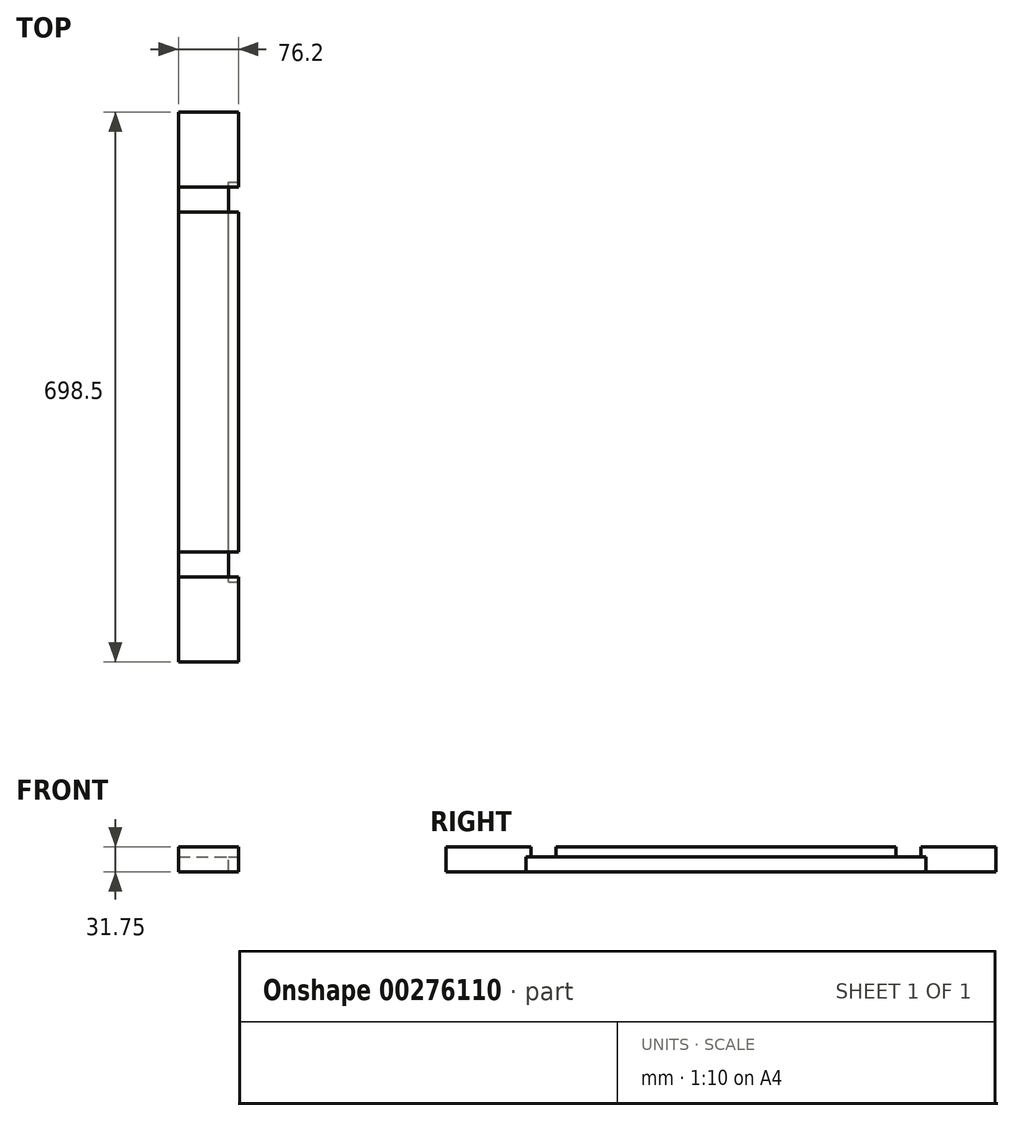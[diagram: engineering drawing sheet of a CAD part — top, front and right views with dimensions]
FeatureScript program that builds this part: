
annotation { "Feature Type Name" : "Feature", "Feature Type Description" : "" }
export const myFeature = defineFeature(function(context is Context, id is Id, definition is map)
    precondition{}
    {
        {
            var Q0;
            Q0=qCreatedBy(makeId("Front.planeOp"),FACE);
            var sketch = newSketch(context, id + "F0", { "sketchPlane" : qUnion([Q0])});
            skLineSegment(sketch, "E0.bottom", {"start": v(0, 0) * mm, "end": v(-76.2, 0) * mm});
            skLineSegment(sketch, "E0.top", {"start": v(0, 31.75) * mm, "end": v(-76.2, 31.75) * mm});
            skLineSegment(sketch, "E0.left", {"start": v(0, 0) * mm, "end": v(0, 31.75) * mm});
            skLineSegment(sketch, "E0.right", {"start": v(-76.2, 0) * mm, "end": v(-76.2, 31.75) * mm});
            skSolve(sketch);
        }
        {
            var Q0;
            Q0=makeQuery(id+"F0.imprint","IMPRINT",FACE,{"disambiguationData":[TD([[makeQuery(id+"F0.imprint","IMPRINT",EDGE,{"derivedFrom":sQuery(id+"F0.wireOp",EDGE,"E0.bottom")}),-1.0]])]});
            extrude(context, id + "F1", {"entities" : qUnion([Q0]), "depth" : 698.5 * mm});
        }
        {
            var Q0;
            Q0=makeQuery(id+"F1.opExtrude","SWEPT_FACE",FACE,{"disambiguationData":[OSD([sQuery(id+"F0.wireOp",EDGE,"E0.left")])]});
            var sketch = newSketch(context, id + "F2", { "sketchPlane" : qUnion([Q0])});
            skLineSegment(sketch, "E1.bottom", {"start": v(-596.9, 0) * mm, "end": v(-88.9, 0) * mm});
            skLineSegment(sketch, "E1.top", {"start": v(-596.9, 19.05) * mm, "end": v(-88.9, 19.05) * mm});
            skLineSegment(sketch, "E1.left", {"start": v(-596.9, 0) * mm, "end": v(-596.9, 19.05) * mm});
            skLineSegment(sketch, "E1.right", {"start": v(-88.9, 0) * mm, "end": v(-88.9, 19.05) * mm});
            skSolve(sketch);
        }
        {
            var Q0;
            Q0=makeQuery(id+"F2.imprint","IMPRINT",FACE,{"disambiguationData":[TD([[makeQuery(id+"F2.imprint","IMPRINT",EDGE,{"derivedFrom":sQuery(id+"F2.wireOp",EDGE,"E1.bottom")}),1.0]])]});
            extrude(context, id + "F3", {"entities" : qUnion([Q0]), "operationType" : NewBodyOperationType.REMOVE, "oppositeDirection" : true, "depth" : 12.7 * mm});
        }
        {
            var Q0;
            Q0=makeQuery(id+"F1.opExtrude","SWEPT_FACE",FACE,{"disambiguationData":[OSD([sQuery(id+"F0.wireOp",EDGE,"E0.top")])]});
            var sketch = newSketch(context, id + "F4", { "sketchPlane" : qUnion([Q0])});
            skLineSegment(sketch, "E2", {"start": v(-76.2, -590.55) * mm, "end": v(0, -590.55) * mm});
            skLineSegment(sketch, "E3", {"start": v(-76.2, -558.8) * mm, "end": v(0, -558.8) * mm});
            skLineSegment(sketch, "E4", {"start": v(-76.2, -95.25) * mm, "end": v(0, -95.25) * mm});
            skLineSegment(sketch, "E5", {"start": v(-76.2, -127) * mm, "end": v(0, -127) * mm});
            skSolve(sketch);
        }
        {
            var Q0;
            {var subQ0=sQuery(id+"F4.wireOp",EDGE,"E2");Q0=makeQuery(id+"F4.imprint","IMPRINT",FACE,{"disambiguationData":[TD([[makeQuery(id+"F4.imprint","IMPRINT",EDGE,{"derivedFrom":subQ0}),1.0]])]});}
            var Q1;
            {var subQ0=sQuery(id+"F4.wireOp",EDGE,"E4");Q1=makeQuery(id+"F4.imprint","IMPRINT",FACE,{"disambiguationData":[TD([[makeQuery(id+"F4.imprint","IMPRINT",EDGE,{"derivedFrom":subQ0}),-1.0]])]});}
            extrude(context, id + "F5", {"entities" : qUnion([Q0, Q1]), "operationType" : NewBodyOperationType.REMOVE, "oppositeDirection" : true, "depth" : 12.7 * mm});
        }
    });
